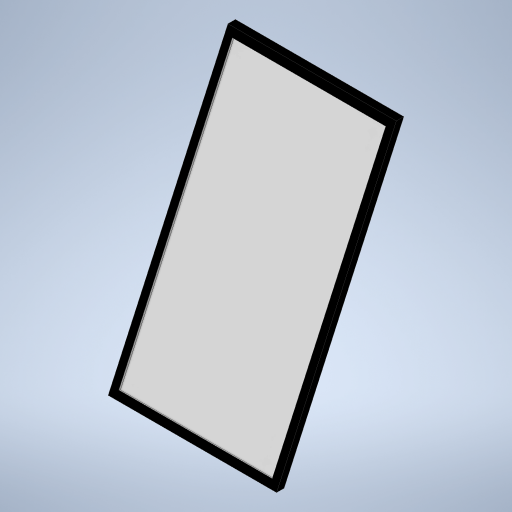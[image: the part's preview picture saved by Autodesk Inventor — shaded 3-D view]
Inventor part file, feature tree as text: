
AUTODESK INVENTOR PART (.ipt)
format: ipt  version: 2024 (Build 280153000, 153)  size: 248,320 bytes
history: native  units: in
note: dims shown in document units (in); Inventor stores cm internally (conversion verified against a paired STEP export)
features: extrude x2, sketch x2
ambient origin geometry x8: Origin, YZ Plane, XZ Plane, XY Plane, X Axis, Y Axis, Z Axis, Center Point
bodies: Body1 (feature_tree)
feature tree (4):
  extrude  "Extrusion2"  Depth=2.0in
  extrude  "Extrusion3"  Depth=0.5in
  sketch  "Sketch2"  dims[d4=70.0in d5=2.0in]
  sketch  "Sketch3"  dims[d6=2.0in d7=32.0in d8=45.0in d9=0.0in d10=2.0in d11=2.0in d12=2.0in d13=2.0in d14=0.5in d15=0.0in]
